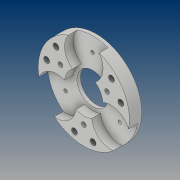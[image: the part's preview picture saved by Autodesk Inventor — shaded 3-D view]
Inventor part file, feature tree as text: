
AUTODESK INVENTOR PART (.ipt)
format: ipt  version: 2021 (Build 250183000, 183)  size: 245,248 bytes
history: native  units: mm
features: sketch x10, extrude x8, pattern_circular x6, thread x6, other x2, plane x2, revolve x2
ambient origin geometry x8: Origin, YZ Plane, XZ Plane, XY Plane, X Axis, Y Axis, Z Axis, Center Point
bodies: Solid1 (feature_tree)
feature tree (36):
  extrude  "Extrusion1"  Depth=53.0mm TaperAngle=0.0deg
  extrude  "Extrusion2"  Depth=165.0mm
  pattern_circular  "Circular Pattern1"  Count=3 Angle=360.0deg
  extrude  "Extrusion3"  Depth=38.0mm TaperAngle=0.0deg
  extrude  "Extrusion4"  Depth=15.0mm
  pattern_circular  "Circular Pattern2"  Count=3 Angle=360.0deg
  extrude  "Extrusion5"  Depth=25.0mm TaperAngle=0.0deg
  extrude  "Extrusion10"  Depth=115.0mm
  pattern_circular  "Circular Pattern7"  Count=5  [1 undecoded]
  extrude  "Extrusion11"  Depth=40.0mm
  pattern_circular  "Circular Pattern8"  Count=4  [1 undecoded]
  thread  "Thread16"  [1 undecoded]
  thread  "Thread17"  [1 undecoded]
  thread  "Thread18"  [1 undecoded]
  thread  "Thread19"  [1 undecoded]
  thread  "Thread20"  [1 undecoded]
  thread  "Thread21"  [1 undecoded]
  other  "Work Axis3"
  plane  "Work Plane2"
  revolve  "Revolution1"  [1 undecoded]
  pattern_circular  "Circular Pattern9"  Count=8  [1 undecoded]
  other  "Work Axis4"
  plane  "Work Plane3"
  revolve  "Revolution2"  [1 undecoded]
  pattern_circular  "Circular Pattern10"  Count=2  [1 undecoded]
  sketch  "Sketch1"  dims[d0=390.0mm d1=53.0mm d2=0.0mm]
  sketch  "Sketch2"  dims[d3=133.838mm d4=165.0mm]
  sketch  "Sketch3"  dims[d5=38.0mm d6=0.0mm d7=30.0mm d8=360.0deg]
  sketch  "Sketch4"  dims[d10=165.0mm d11=38.0mm d12=0.0mm]
  sketch  "Sketch6"  dims[d13=15.0mm d14=133.838mm]
  sketch  "Sketch12"  dims[d15=25.0mm d16=0.0mm d17=30.0mm d18=360.0deg]
  sketch  "Sketch13"  dims[d20=135.0mm d21=25.0mm d22=0.0mm]
  sketch  "Sketch15"  dims[d90=30.0mm d91=360.0deg d93=25.0mm d94=40.0mm d95=160.0mm d96=25.0mm d97=40.0mm d98=160.0mm d99=40.0mm d100=0.0mm d101=30.0mm d102=360.0deg]
  sketch  "Sketch16"  dims[d105=0.0mm d106=80.0mm d107=1.256638mm d108=6.0mm d109=4.0mm d110=10.0mm d111=80.0mm d112=4.0mm d113=20.0mm d114=10.0mm d115=0.0mm d116=10.0mm d117=0.0mm d118=10.0mm d119=0.0mm d120=10.0mm d121=0.0mm d122=10.0mm d123=0.0mm d124=10.0mm d125=0.0mm d126=45.25mm d127=90.0deg d128=30.0mm d129=360.0deg d131=-118.5mm d132=90.0deg d133=30.0mm d134=360.0deg]
  sketch  "Sketch14"  dims[d86=20.0mm d87=115.0mm d88=50.0mm d89=0.0mm]
  extrude  "Extrusion12"  Depth=10.0mm TaperAngle=0.0deg
note: 12 required parameter values undecoded (feature->parameter linkage not recoverable at this tier; creation-order binding heuristic only, values carry confidence <= 0.55)